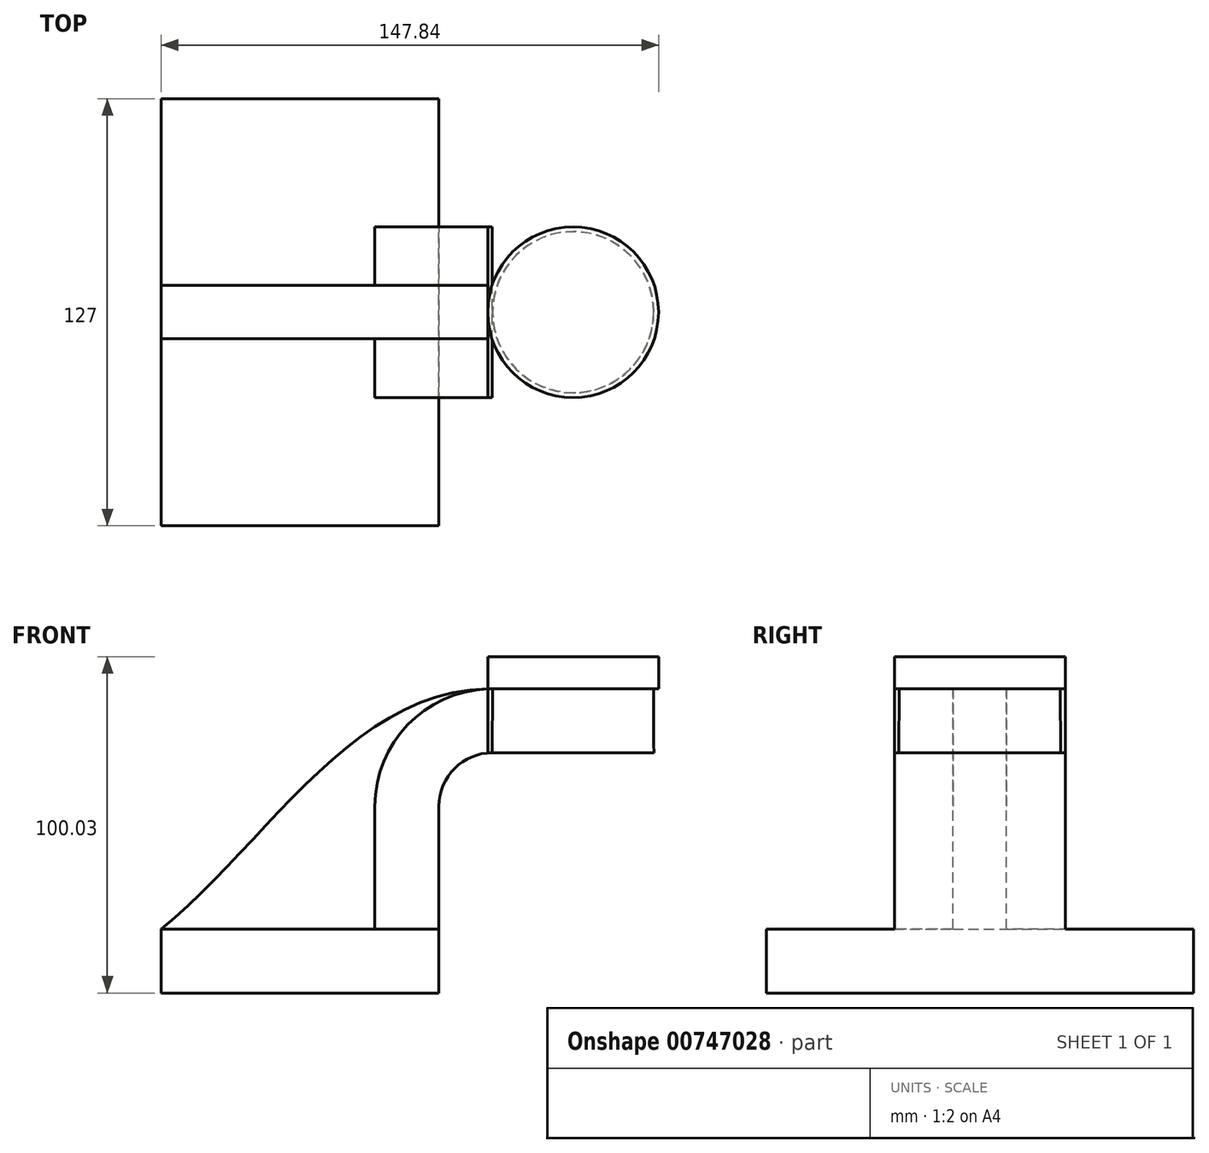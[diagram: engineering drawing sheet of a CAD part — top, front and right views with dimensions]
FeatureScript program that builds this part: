
annotation { "Feature Type Name" : "Feature", "Feature Type Description" : "" }
export const myFeature = defineFeature(function(context is Context, id is Id, definition is map)
    precondition{}
    {
        {
            var Q0;
            Q0=qCreatedBy(makeId("Front.planeOp"),FACE);
            var sketch = newSketch(context, id + "F0", { "sketchPlane" : qUnion([Q0])});
            skLineSegment(sketch, "E0.bottom", {"start": v(41.28, -9.52) * mm, "end": v(-41.28, -9.53) * mm});
            skLineSegment(sketch, "E0.top", {"start": v(41.28, 9.53) * mm, "end": v(-41.28, 9.52) * mm});
            skLineSegment(sketch, "E0.left", {"start": v(41.28, -9.52) * mm, "end": v(41.28, 9.53) * mm});
            skLineSegment(sketch, "E0.right", {"start": v(-41.28, -9.53) * mm, "end": v(-41.28, 9.52) * mm});
            skPoint(sketch, "E0.middle", {"position": v(0, 0) * mm});
            skLineSegment(sketch, "E1.bottom", {"start": v(55.76, 61.93) * mm, "end": v(106.56, 61.93) * mm});
            skLineSegment(sketch, "E1.top", {"start": v(55.76, 90.5) * mm, "end": v(106.56, 90.5) * mm});
            skLineSegment(sketch, "E1.left", {"start": v(55.76, 61.93) * mm, "end": v(55.76, 90.5) * mm});
            skLineSegment(sketch, "E1.right", {"start": v(106.56, 61.93) * mm, "end": v(106.56, 90.5) * mm});
            skPoint(sketch, "E1.middle", {"position": v(81.16, 76.21) * mm});
            skLineSegment(sketch, "E2", {"start": v(41.28, 9.53) * mm, "end": v(41.28, 46.05) * mm});
            skArc(sketch, "E3", {"start": v(41.28, 46.05) * mm, "mid": v(45.92, 57.28) * mm, "end": v(57.15, 61.93) * mm});
            skLineSegment(sketch, "E4", {"start": v(57.15, 61.93) * mm, "end": v(81.16, 61.93) * mm});
            skArc(sketch, "E5.0", {"start": v(22.22, 46.05) * mm, "mid": v(32.5, 70.78) * mm, "end": v(57.26, 80.98) * mm});
            skLineSegment(sketch, "E5.1", {"start": v(22.22, 9.53) * mm, "end": v(22.22, 46.05) * mm});
            skLineSegment(sketch, "E6", {"start": v(57.26, 80.98) * mm, "end": v(57.15, 61.93) * mm});
            skFitSpline(sketch, "E7", {"points": [v(-41.28, 9.52) * mm, v(55.76, 80.98) * mm], "startDerivative": vector(92.27, 74.63) * mm, "endDerivative": vector(122.42, 2.18) * mm});
            skLineSegment(sketch, "E8", {"start": v(81.16, 90.5) * mm, "end": v(81.16, 61.93) * mm});
            skSolve(sketch);
        }
        {
            var Q0;
            Q0=makeQuery(id+"F0.imprint","IMPRINT",FACE,{"disambiguationData":[TD([[makeQuery(id+"F0.imprint","IMPRINT",EDGE,{"derivedFrom":sQuery(id+"F0.wireOp",EDGE,"E0.bottom")}),-1.0]])]});
            extrude(context, id + "F1", {"entities" : qUnion([Q0]), "endBound" : BoundingType.SYMMETRIC, "oppositeDirection" : true, "depth" : 127 * mm, "offsetDistance" : 25.4 * mm});
        }
        {
            var Q0;
            {var subQ0=sQuery(id+"F0.wireOp",EDGE,"E2");Q0=makeQuery(id+"F0.imprint","IMPRINT",FACE,{"disambiguationData":[TD([[makeQuery(id+"F0.imprint","IMPRINT",EDGE,{"derivedFrom":subQ0}),1.0]])]});}
            extrude(context, id + "F2", {"entities" : qUnion([Q0]), "operationType" : NewBodyOperationType.ADD, "endBound" : BoundingType.SYMMETRIC, "depth" : 50.8 * mm, "offsetDistance" : 25.4 * mm});
        }
        {
            var Q0;
            {var subQ0=sQuery(id+"F0.wireOp",EDGE,"E5.1");Q0=makeQuery(id+"F0.imprint","IMPRINT",FACE,{"disambiguationData":[TD([[makeQuery(id+"F0.imprint","IMPRINT",EDGE,{"derivedFrom":subQ0}),1.0]])]});}
            extrude(context, id + "F3", {"entities" : qUnion([Q0]), "operationType" : NewBodyOperationType.ADD, "endBound" : BoundingType.SYMMETRIC, "depth" : 15.88 * mm, "offsetDistance" : 25.4 * mm});
        }
        {
            var Q0;
            {var subQ8=sQuery(id+"F0.wireOp",EDGE,"E6");Q0=makeQuery(id+"F0.imprint","IMPRINT",FACE,{"disambiguationData":[TD([[makeQuery(id+"F0.imprint","IMPRINT",EDGE,{"derivedFrom":subQ8}),1.0]])]});}
            var Q1;
            Q1=sQuery(id+"F0.wireOp",EDGE,"E8");
            revolve(context, id + "F4", {"surfaceOperationType" : NewSurfaceOperationType.NEW, "entities" : qUnion([Q0]), "axis" : qUnion([Q1]), "revolveType" : RevolveType.FULL});
        }
    });
